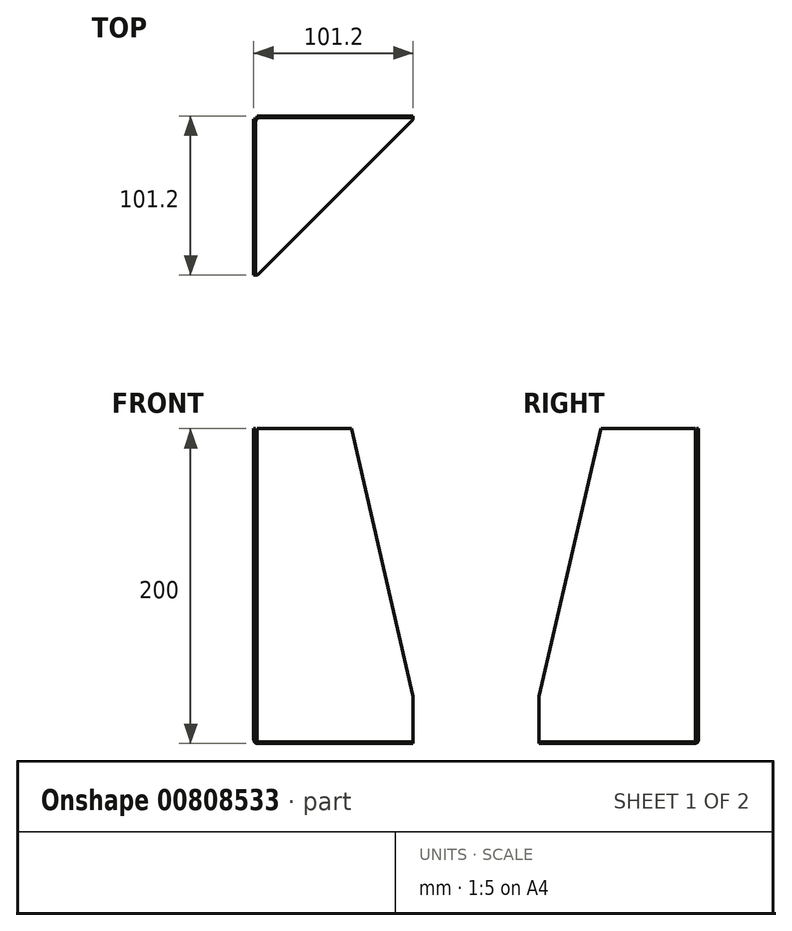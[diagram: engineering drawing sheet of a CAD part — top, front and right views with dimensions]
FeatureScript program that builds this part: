
annotation { "Feature Type Name" : "Feature", "Feature Type Description" : "" }
export const myFeature = defineFeature(function(context is Context, id is Id, definition is map)
    precondition{}
    {
        {
            var Q0;
            Q0=qCreatedBy(makeId("Top.planeOp"),FACE);
            var sketch = newSketch(context, id + "F0", { "sketchPlane" : qUnion([Q0])});
            skLineSegment(sketch, "E0.bottom", {"start": v(50.6, -50.6) * mm, "end": v(-50.6, -50.6) * mm});
            skLineSegment(sketch, "E0.top", {"start": v(50.6, 50.6) * mm, "end": v(-50.6, 50.6) * mm});
            skLineSegment(sketch, "E0.left", {"start": v(50.6, -50.6) * mm, "end": v(50.6, 50.6) * mm});
            skLineSegment(sketch, "E0.right", {"start": v(-50.6, -50.6) * mm, "end": v(-50.6, 50.6) * mm});
            skPoint(sketch, "E0.middle", {"position": v(0, 0) * mm});
            skSolve(sketch);
        }
        {
            var Q0;
            Q0 = qSketchRegion(id + "F0", true);
            extrude(context, id + "F1", {"entities" : qUnion([Q0]), "depth" : 200 * mm, "offsetDistance" : 25 * mm});
        }
        {
            var Q0;
            Q0=makeQuery(id+"F1.opExtrude","CAP_FACE",FACE,{"disambiguationData":[OSD([sQuery(id+"F0.wireOp",EDGE,"E0.bottom"),sQuery(id+"F0.wireOp",EDGE,"E0.top"),sQuery(id+"F0.wireOp",EDGE,"E0.left"),sQuery(id+"F0.wireOp",EDGE,"E0.right")])],"isStart":false});
            var Q1;
            Q1=makeQuery(id+"F1.opExtrude","SWEPT_FACE",FACE,{"disambiguationData":[OSD([sQuery(id+"F0.wireOp",EDGE,"E0.bottom")])]});
            var Q2;
            Q2=makeQuery(id+"F1.opExtrude","SWEPT_FACE",FACE,{"disambiguationData":[OSD([sQuery(id+"F0.wireOp",EDGE,"E0.left")])]});
            shell(context, id + "F2", {"entities" : qUnion([Q0, Q1, Q2]), "thickness" : 1.2 * mm});
        }
        {
            var Q0;
            Q0=makeQuery(id+"F1.opExtrude","CAP_FACE",FACE,{"disambiguationData":[OSD([sQuery(id+"F0.wireOp",EDGE,"E0.bottom"),sQuery(id+"F0.wireOp",EDGE,"E0.top"),sQuery(id+"F0.wireOp",EDGE,"E0.left"),sQuery(id+"F0.wireOp",EDGE,"E0.right")])],"isStart":true});
            var sketch = newSketch(context, id + "F3", { "sketchPlane" : qUnion([Q0])});
            skLineSegment(sketch, "E1.bottom", {"start": v(-50.6, -50.6) * mm, "end": v(-49.4, -50.6) * mm});
            skLineSegment(sketch, "E1.top", {"start": v(-50.6, -49.4) * mm, "end": v(-49.4, -49.4) * mm});
            skLineSegment(sketch, "E1.left", {"start": v(-50.6, -50.6) * mm, "end": v(-50.6, -49.4) * mm});
            skLineSegment(sketch, "E1.right", {"start": v(-49.4, -50.6) * mm, "end": v(-49.4, -49.4) * mm});
            skSolve(sketch);
        }
        {
            var Q0;
            Q0=makeQuery(id+"F1.opExtrude","CAP_FACE",FACE,{"disambiguationData":[OSD([sQuery(id+"F0.wireOp",EDGE,"E0.bottom"),sQuery(id+"F0.wireOp",EDGE,"E0.top"),sQuery(id+"F0.wireOp",EDGE,"E0.left"),sQuery(id+"F0.wireOp",EDGE,"E0.right")])],"isStart":false});
            var sketch = newSketch(context, id + "F4", { "sketchPlane" : qUnion([Q0])});
            skLineSegment(sketch, "E2", {"start": v(-50.6, 48.6) * mm, "end": v(-50.6, 50.6) * mm});
            skLineSegment(sketch, "E3", {"start": v(-50.6, 50.6) * mm, "end": v(-48.6, 50.6) * mm});
            skLineSegment(sketch, "E4", {"start": v(-50.6, 48.6) * mm, "end": v(-48.6, 48.6) * mm});
            skLineSegment(sketch, "E5", {"start": v(-48.6, 48.6) * mm, "end": v(-48.6, 50.6) * mm});
            skSolve(sketch);
        }
        {
            var Q0;
            {var subQ0=sQuery(id+"F4.wireOp",EDGE,"E5");var subQ1=sQuery(id+"F4.wireOp",EDGE,"E4");var subQ2=makeQuery(id+"F4.imprint","INTERSECT",VERTEX,{"derivedFrom":[subQ1,subQ0]});Q0=makeQuery(id+"F4.imprint","IMPRINT",FACE,{"disambiguationData":[TD([[makeQuery(id+"F4.imprint","IMPRINT",EDGE,{"disambiguationData":[TD([[subQ2,1.0]])],"derivedFrom":subQ1}),1.0]])]});}
            var Q1;
            {var subQ1=sQuery(id+"F4.wireOp",EDGE,"E2");Q1=makeQuery(id+"F4.imprint","IMPRINT",FACE,{"disambiguationData":[TD([[makeQuery(id+"F4.imprint","IMPRINT",EDGE,{"derivedFrom":subQ1}),-1.0]])]});}
            extrude(context, id + "F5", {"entities" : qUnion([Q0, Q1]), "operationType" : NewBodyOperationType.REMOVE, "endBound" : BoundingType.THROUGH_ALL, "oppositeDirection" : true, "depth" : 25 * mm, "offsetDistance" : 25 * mm});
        }
        {
            var Q0;
            {var subQ0=sQuery(id+"F0.wireOp",EDGE,"E0.top");Q0=makeQuery(id+"F2.opShell","OFFSET_EDGE",EDGE,{"disambiguationData":[OSD([subQ0]),TDD([makeQuery(id+"F1.opExtrude","CAP_EDGE",EDGE,{"disambiguationData":[OSD([subQ0])],"isStart":true})])]});}
            fillet(context, id + "F6", {"entities" : qUnion([Q0]), "radius" : 1.2 * mm, "allowEdgeOverflow" : false});
        }
        {
            var Q0;
            {var subQ0=sQuery(id+"F0.wireOp",EDGE,"E0.right");Q0=makeQuery(id+"F2.opShell","OFFSET_EDGE",EDGE,{"disambiguationData":[OSD([subQ0]),TDD([makeQuery(id+"F1.opExtrude","CAP_EDGE",EDGE,{"disambiguationData":[OSD([subQ0])],"isStart":true})])]});}
            fillet(context, id + "F7", {"entities" : qUnion([Q0]), "radius" : 1.2 * mm, "tangentPropagation" : true, "allowEdgeOverflow" : false});
        }
        {
            var Q0;
            Q0=makeQuery(id+"F1.opExtrude","CAP_EDGE",EDGE,{"disambiguationData":[OSD([sQuery(id+"F0.wireOp",EDGE,"E0.right")])],"isStart":true});
            fillet(context, id + "F8", {"entities" : qUnion([Q0]), "radius" : 2.4 * mm, "tangentPropagation" : true, "allowEdgeOverflow" : false});
        }
        {
            var Q0;
            Q0=makeQuery(id+"F1.opExtrude","CAP_EDGE",EDGE,{"disambiguationData":[OSD([sQuery(id+"F0.wireOp",EDGE,"E0.top")])],"isStart":true});
            fillet(context, id + "F9", {"entities" : qUnion([Q0]), "radius" : 2.4 * mm, "tangentPropagation" : true, "allowEdgeOverflow" : false});
        }
        {
            var Q0;
            Q0=makeQuery(id+"F1.opExtrude","SWEPT_FACE",FACE,{"disambiguationData":[OSD([sQuery(id+"F0.wireOp",EDGE,"E0.right")])]});
            var sketch = newSketch(context, id + "F10", { "sketchPlane" : qUnion([Q0])});
            skLineSegment(sketch, "E6", {"start": v(50.6, 200) * mm, "end": v(50.6, 30) * mm});
            skLineSegment(sketch, "E7", {"start": v(50.6, 30) * mm, "end": v(11.4, 200) * mm});
            skLineSegment(sketch, "E8", {"start": v(11.4, 200) * mm, "end": v(50.6, 200) * mm});
            skSolve(sketch);
        }
        {
            var Q0;
            Q0=makeQuery(id+"F1.opExtrude","SWEPT_FACE",FACE,{"disambiguationData":[OSD([sQuery(id+"F0.wireOp",EDGE,"E0.top")])]});
            var sketch = newSketch(context, id + "F11", { "sketchPlane" : qUnion([Q0])});
            skLineSegment(sketch, "E9", {"start": v(-50.6, 200) * mm, "end": v(-11.4, 200) * mm});
            skLineSegment(sketch, "E10", {"start": v(-11.4, 200) * mm, "end": v(-50.6, 30) * mm});
            skLineSegment(sketch, "E11", {"start": v(-50.6, 30) * mm, "end": v(-50.6, 200) * mm});
            skSolve(sketch);
        }
        {
            var Q0;
            Q0=makeQuery(id+"F11.imprint","IMPRINT",FACE,{"disambiguationData":[TD([[makeQuery(id+"F11.imprint","IMPRINT",EDGE,{"derivedFrom":sQuery(id+"F11.wireOp",EDGE,"E9")}),-1.0]])]});
            extrude(context, id + "F12", {"entities" : qUnion([Q0]), "operationType" : NewBodyOperationType.REMOVE, "oppositeDirection" : true, "depth" : 25 * mm, "offsetDistance" : 25 * mm});
        }
        {
            var Q0;
            Q0 = qSketchRegion(id + "F10", true);
            extrude(context, id + "F13", {"entities" : qUnion([Q0]), "operationType" : NewBodyOperationType.REMOVE, "oppositeDirection" : true, "depth" : 25 * mm, "offsetDistance" : 25 * mm});
        }
        {
            var Q0;
            {var subQ4=sQuery(id+"F3.wireOp",EDGE,"E1.top");Q0=makeQuery(id+"F3.imprint","IMPRINT",FACE,{"disambiguationData":[TD([[makeQuery(id+"F3.imprint","IMPRINT",EDGE,{"derivedFrom":subQ4}),1.0]])]});}
            var sketch = newSketch(context, id + "F14", { "sketchPlane" : qUnion([Q0])});
            skLineSegment(sketch, "E12.0", {"start": v(50.6, 50.6) * mm, "end": v(-48.2, 50.6) * mm});
            skLineSegment(sketch, "E13.0", {"start": v(50.6, 50.6) * mm, "end": v(50.6, -48.2) * mm});
            skLineSegment(sketch, "E14", {"start": v(-48.2, 50.6) * mm, "end": v(50.6, -48.2) * mm});
            skSolve(sketch);
        }
        {
            var Q0;
            Q0 = qSketchRegion(id + "F14", true);
            extrude(context, id + "F15", {"entities" : qUnion([Q0]), "operationType" : NewBodyOperationType.REMOVE, "oppositeDirection" : true, "depth" : 25 * mm, "offsetDistance" : 25 * mm});
        }
    });
